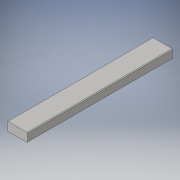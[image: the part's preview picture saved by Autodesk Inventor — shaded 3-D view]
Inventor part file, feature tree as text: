
AUTODESK INVENTOR PART (.ipt)
format: ipt  version: 2016 (Build 200138000, 138)  size: 96,768 bytes
history: native  units: in
note: dims shown in document units (in); Inventor stores cm internally (conversion verified against a paired STEP export)
features: extrude x1, fillet x1, sketch x1
ambient origin geometry x8: Origin, YZ Plane, XZ Plane, XY Plane, X Axis, Y Axis, Z Axis, Center Point
bodies: Solid1 (feature_tree)
feature tree (3):
  extrude  "Extrusion1"  Depth=1.5in
  fillet  "Fillet1"  Radius=25.0in
  sketch  "Sketch1"  dims[d0=3.5in d1=1.5in d2=25.0in d3=0.0in d4=0.125in]
